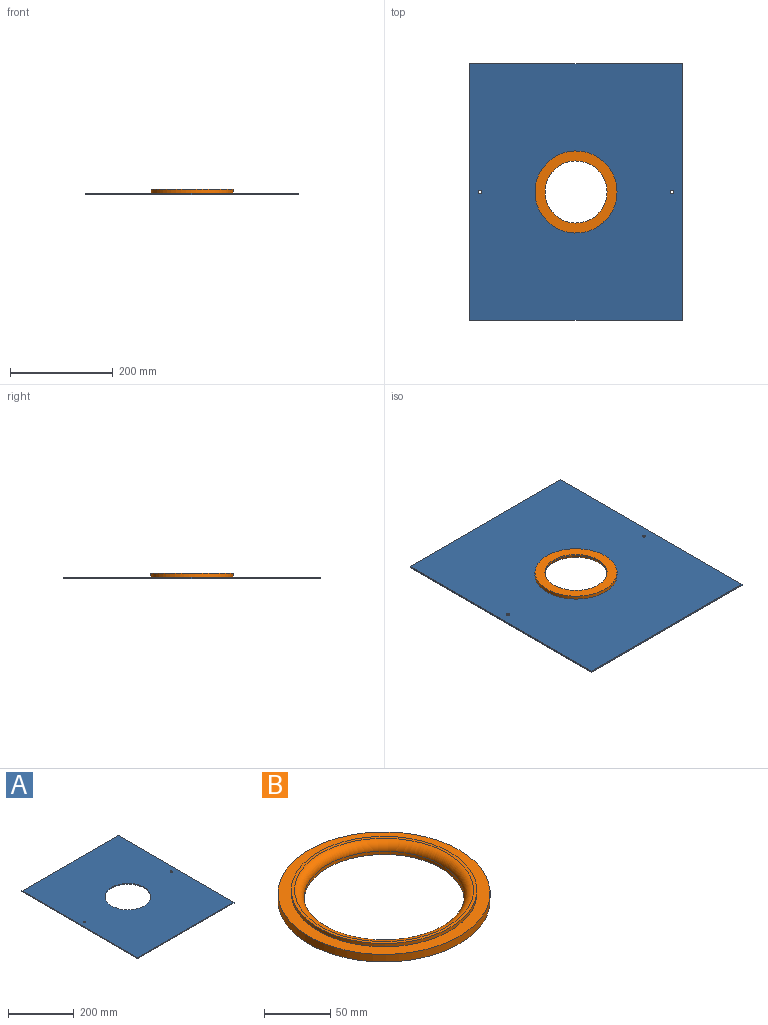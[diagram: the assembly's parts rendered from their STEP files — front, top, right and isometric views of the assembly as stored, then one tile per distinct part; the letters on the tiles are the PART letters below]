
ASSEMBLY  parts=2 mates=1
PART A: 9 faces, bbox 415x500x3 mm
  f0: plane 500x3mm, normal (-1,0,0), area 1500mm2, adj f1,f3,f4,f5
  f1: plane 415x3mm, normal (0,-1,0), area 1245mm2, adj f0,f2,f4,f5
  f2: plane 500x3mm, normal (1,0,0), area 1500mm2, adj f1,f3,f4,f5
  f3: plane 415x3mm, normal (0,1,0), area 1245mm2, adj f0,f2,f4,f5
  f4: plane 500x415mm, normal (0,0,1), area 192037.8mm2, adj f0,f1,f2,f3,f6,f7,f8
  f5: plane 500x415mm, normal (0,0,-1), area 192037.8mm2, adj f0,f1,f2,f3,f6,f7,f8
  f6: cylinder r=3.3mm len=6.6mm, axis (0,0,1), area 62.2mm2, adj f4,f5
  f7: cylinder r=3.3mm len=6.6mm, axis (0,0,1), area 62.2mm2, adj f4,f5
  f8: cylinder r=70mm len=140mm, axis (0,0,1), area 1319.5mm2, adj f4,f5
PART B: 7 faces, bbox 160x160x12 mm
  f0: cylinder r=80mm len=160mm, axis (0,0,-1), area 3518.6mm2, adj f3,f6
  f1: plane 140x140mm, normal (0,0,1), area 1079.9mm2, adj f4,f5
  f2: cylinder r=60.5mm len=121mm, axis (0,0,-1), area 1140.4mm2, adj f3,f4
  f3: plane 160x160mm, normal (0,0,-1), area 8607.2mm2, adj f0,f2
  f4: torus R=67.5mm, axis (0,0,1), area 4355.5mm2, adj f1,f2
  f5: cylinder r=70mm len=140mm, axis (0,0,1), area 1319.5mm2, adj f1,f6
  f6: plane 160x160mm, normal (0,0,1), area 4712.4mm2, adj f0,f5
PLACE A at identity
PLACE B rot(axis=(1,0,0),180deg) t=(207.5,250,10)mm
MATE revolute B.f5 <-> A.f8  axis (0,0,-1) through (207.5,250,3)mm
